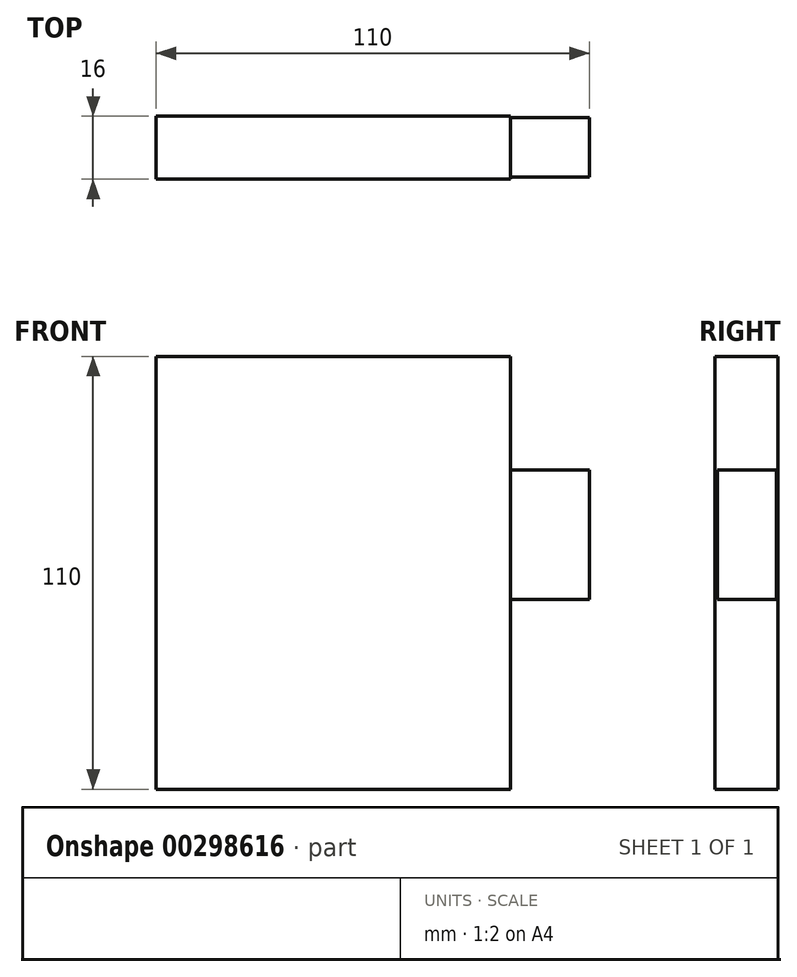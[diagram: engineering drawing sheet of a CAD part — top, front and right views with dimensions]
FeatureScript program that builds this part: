
annotation { "Feature Type Name" : "Feature", "Feature Type Description" : "" }
export const myFeature = defineFeature(function(context is Context, id is Id, definition is map)
    precondition{}
    {
        {
            var Q0;
            Q0=qCreatedBy(makeId("Front.planeOp"),FACE);
            var sketch = newSketch(context, id + "F0", { "sketchPlane" : qUnion([Q0])});
            skLineSegment(sketch, "E0.bottom", {"start": v(-56.68, 52.41) * mm, "end": v(33.32, 52.41) * mm});
            skLineSegment(sketch, "E0.top", {"start": v(-56.68, -57.59) * mm, "end": v(33.32, -57.59) * mm});
            skLineSegment(sketch, "E0.left", {"start": v(-56.68, 52.41) * mm, "end": v(-56.68, -57.59) * mm});
            skLineSegment(sketch, "E0.right", {"start": v(33.32, 52.41) * mm, "end": v(33.32, -57.59) * mm});
            skSolve(sketch);
        }
        {
            var Q0;
            Q0 = qSketchRegion(id + "F0", true);
            extrude(context, id + "F1", {"entities" : qUnion([Q0]), "depth" : 16 * mm});
        }
        {
            var Q0;
            Q0=makeQuery(id+"F1.opExtrude","SWEPT_FACE",FACE,{"disambiguationData":[OSD([sQuery(id+"F0.wireOp",EDGE,"E0.right")])]});
            var sketch = newSketch(context, id + "F2", { "sketchPlane" : qUnion([Q0])});
            skLineSegment(sketch, "E1.bottom", {"start": v(-0.4, -9.4) * mm, "end": v(-15.4, -9.4) * mm});
            skLineSegment(sketch, "E1.top", {"start": v(-0.4, 23.6) * mm, "end": v(-15.4, 23.6) * mm});
            skLineSegment(sketch, "E1.left", {"start": v(-0.4, -9.4) * mm, "end": v(-0.4, 23.6) * mm});
            skLineSegment(sketch, "E1.right", {"start": v(-15.4, -9.4) * mm, "end": v(-15.4, 23.6) * mm});
            skPoint(sketch, "E1.middle", {"position": v(-7.9, 7.1) * mm});
            skSolve(sketch);
        }
        {
            var Q0;
            Q0 = qSketchRegion(id + "F2", true);
            extrude(context, id + "F3", {"entities" : qUnion([Q0]), "operationType" : NewBodyOperationType.ADD, "depth" : 20 * mm});
        }
    });
